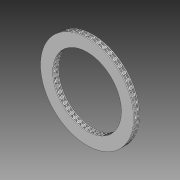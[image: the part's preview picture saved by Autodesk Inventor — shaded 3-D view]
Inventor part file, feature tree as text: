
AUTODESK INVENTOR PART (.ipt)
format: ipt  version: 2020 (Build 240168000, 168)  size: 530,432 bytes
history: native  units: mm
features: sketch x3, revolve x2, extrude x1, pattern_circular x1
ambient origin geometry x8: Origin, YZ Plane, XZ Plane, XY Plane, X Axis, Y Axis, Z Axis, Center Point
bodies: Solid1 (feature_tree)
feature tree (7):
  extrude  "Extrusion1"  Depth=70.0mm
  revolve  "Revolution1"  [1 undecoded]
  pattern_circular  "Circular Pattern1"  Count=50 Angle=360.0deg
  revolve  "Revolution2"  [1 undecoded]
  sketch  "Sketch1"  dims[d0=70.0mm d1=95.0mm]
  sketch  "Sketch2"  dims[d2=1.0mm d3=0.0mm d4=2.0mm]
  sketch  "Sketch3"  dims[d5=90.0deg d6=500.0mm d7=360.0deg d9=1.0mm d10=1.0mm d11=90.0deg]
note: 2 required parameter values undecoded (feature->parameter linkage not recoverable at this tier; creation-order binding heuristic only, values carry confidence <= 0.55)
